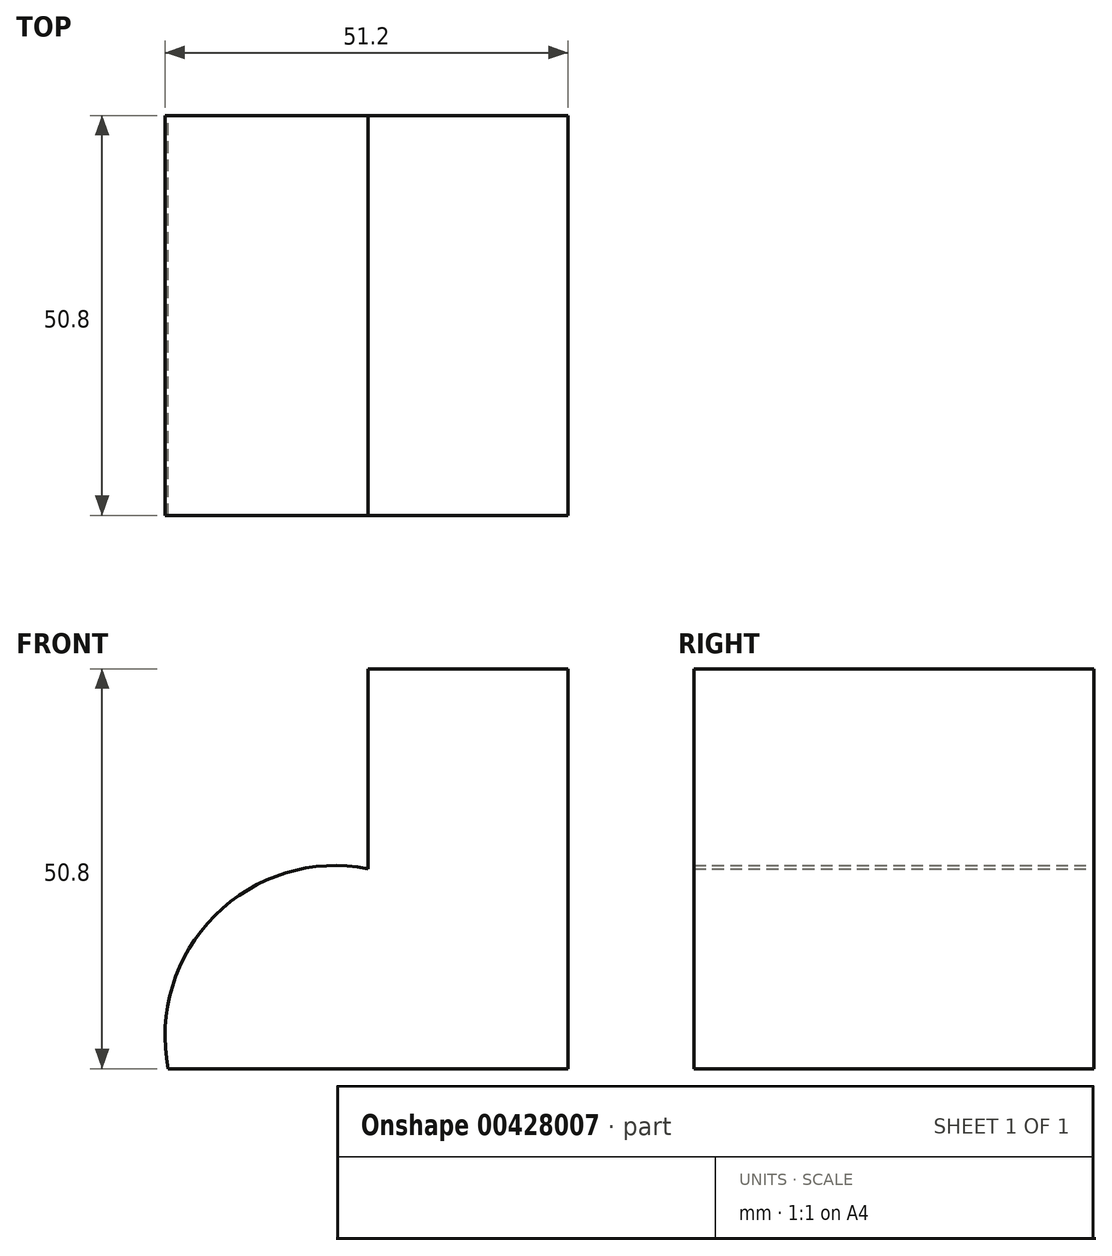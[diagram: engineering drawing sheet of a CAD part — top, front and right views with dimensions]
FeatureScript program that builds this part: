
annotation { "Feature Type Name" : "Feature", "Feature Type Description" : "" }
export const myFeature = defineFeature(function(context is Context, id is Id, definition is map)
    precondition{}
    {
        {
            var Q0;
            Q0=qCreatedBy(makeId("Front.planeOp"),FACE);
            var sketch = newSketch(context, id + "F0", { "sketchPlane" : qUnion([Q0])});
            skArc(sketch, "E0", {"start": v(0, 25.4) * mm, "mid": v(-19.46, 19.46) * mm, "end": v(-25.4, 0) * mm});
            skLineSegment(sketch, "E1", {"start": v(0, 25.4) * mm, "end": v(0, 50.8) * mm});
            skLineSegment(sketch, "E2", {"start": v(0, 50.8) * mm, "end": v(25.4, 50.8) * mm});
            skLineSegment(sketch, "E3", {"start": v(25.4, 50.8) * mm, "end": v(25.4, 0) * mm});
            skLineSegment(sketch, "E4", {"start": v(25.4, 0) * mm, "end": v(-25.4, 0) * mm});
            skSolve(sketch);
        }
        {
            var Q0;
            Q0 = qSketchRegion(id + "F0", true);
            extrude(context, id + "F1", {"entities" : qUnion([Q0]), "depth" : 50.8 * mm});
        }
    });
